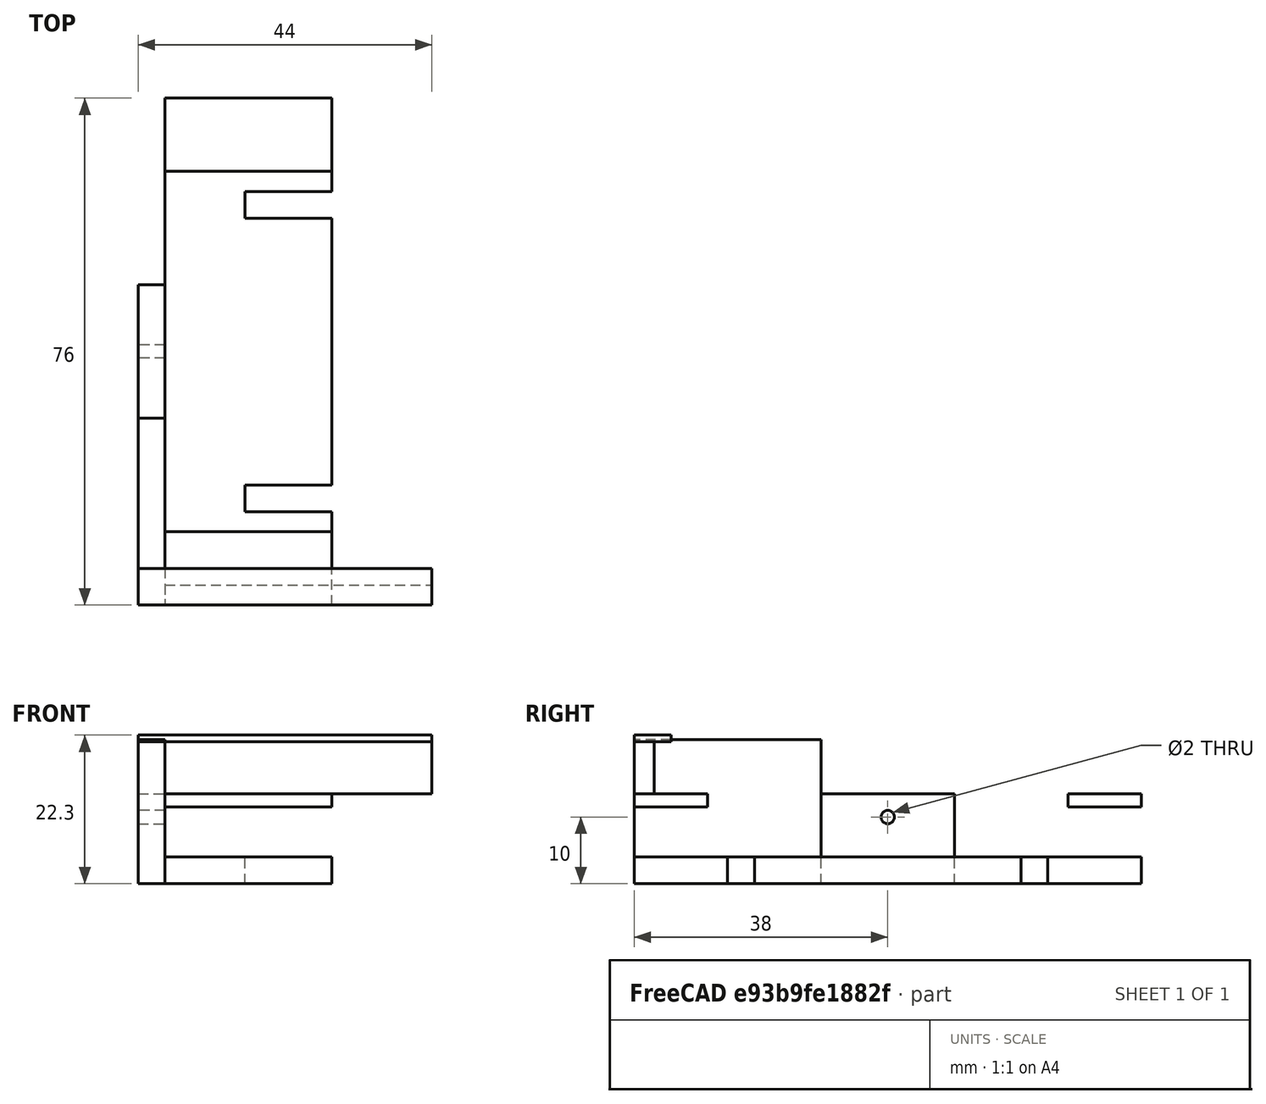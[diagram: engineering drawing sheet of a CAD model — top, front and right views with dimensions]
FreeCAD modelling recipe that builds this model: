
FCSTD DOCUMENT  (FreeCAD 0.21R33771 (Git))
Label: phonestand-s7
License: All rights reserved
LicenseURL: https://en.wikipedia.org/wiki/All_rights_reserved
objects: Part::Box×8, Part::Mirroring×4, Part::Cut×4, Part::Cylinder×1
note: 17 computed .brp shape members not serialized (recipe doc carries the construction recipe); baked Part::Feature solids carry a one-line shape summary decoded from their .brp

FEATURE [Part::Box] Box  label="Groundplate"
  AttacherType = Attacher::AttachEngine3D
  Height = 4
  Length = 25
  Placement = pos=(0,-38,0) rot=(0,0,1;0rad)
  Width = 76
FEATURE [Part::Box] Box001  label="Cube001"
  AttacherType = Attacher::AttachEngine3D
  Height = 9
  Length = 13
  Placement = pos=(12,20,0) rot=(0,0,1;0rad)
  Width = 4
FEATURE [Part::Mirroring] Part__Mirroring  label="Cube001 (Mirror #1)"
  Base = (0,0,0)
  Normal = (0,1,0)
  Source = -> Box001
FEATURE [Part::Cut] Cut
  Base = -> Box
  Tool = -> Box001
FEATURE [Part::Cut] Cut001
  Base = -> Cut
  Tool = -> Part__Mirroring
FEATURE [Part::Box] Box002  label="Backplane"
  AttacherType = Attacher::AttachEngine3D
  Height = 21.6
  Length = 4
  Placement = pos=(-4,10,0) rot=(0,0,1;0rad)
  Width = 28
FEATURE [Part::Box] Box003  label="arm"
  AttacherType = Attacher::AttachEngine3D
  Height = 7.8
  Length = 40
  Placement = pos=(0,35,13.5) rot=(0,0,1;0rad)
  Width = 3
FEATURE [Part::Box] Box004  label="top"
  AttacherType = Attacher::AttachEngine3D
  Height = 1
  Length = 44
  Placement = pos=(-4,32.5,21.3) rot=(0,0,1;0rad)
  Width = 5.5
FEATURE [Part::Box] Box005  label="support"
  AttacherType = Attacher::AttachEngine3D
  Height = 2
  Length = 25
  Placement = pos=(0,-38,11.5) rot=(0,0,1;0rad)
  Width = 76
FEATURE [Part::Mirroring] Part__Mirroring001  label="Backplane (Mirror #2)"
  Base = (0,0,0)
  Normal = (0,1,0)
  Source = -> Box002
FEATURE [Part::Mirroring] Part__Mirroring002  label="arm (Mirror #3)"
  Base = (0,0,0)
  Normal = (0,1,0)
  Source = -> Box003
FEATURE [Part::Mirroring] Part__Mirroring003  label="top (Mirror #4)"
  Base = (0,0,0)
  Normal = (0,1,0)
  Source = -> Box004
FEATURE [Part::Box] Box006  label="Cube"
  AttacherType = Attacher::AttachEngine3D
  Height = 13.5
  Length = 4
  Placement = pos=(-4,-10,0) rot=(0,0,1;0rad)
  Width = 20
FEATURE [Part::Box] Box007  label="Cube002"
  AttacherType = Attacher::AttachEngine3D
  Height = 5
  Length = 25
  Placement = pos=(0,-27,10) rot=(0,0,1;0rad)
  Width = 54
FEATURE [Part::Cut] Cut002
  Base = -> Box005
  Tool = -> Box007
FEATURE [Part::Cylinder] Cylinder
  Angle = 360
  AttacherType = Attacher::AttachEngine3D
  FirstAngle = 0
  Height = 30
  Placement = pos=(-4,0,10) rot=(0,1,0;1.5708rad)
  Radius = 1
  SecondAngle = 0
FEATURE [Part::Cut] Cut003
  Base = -> Box006
  Tool = -> Cylinder
